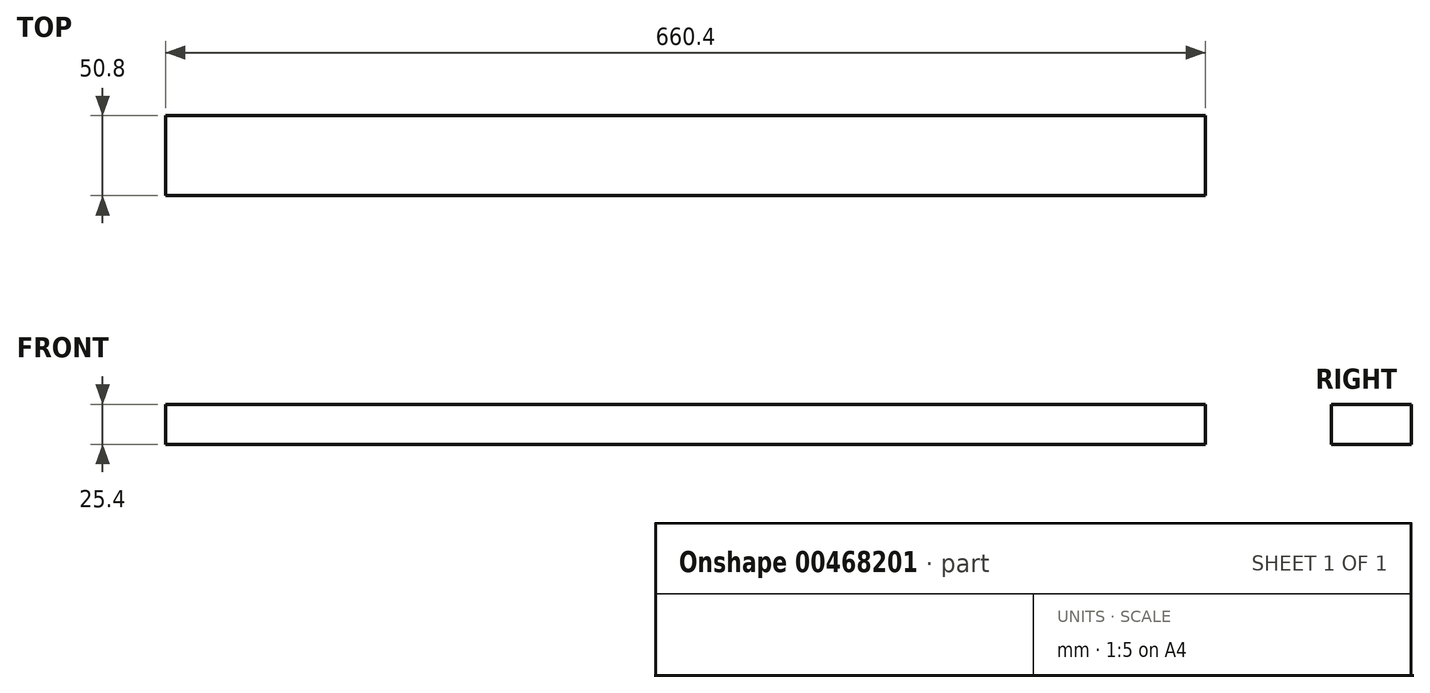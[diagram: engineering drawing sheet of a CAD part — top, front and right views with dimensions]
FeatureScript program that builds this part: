
annotation { "Feature Type Name" : "Feature", "Feature Type Description" : "" }
export const myFeature = defineFeature(function(context is Context, id is Id, definition is map)
    precondition{}
    {
        {
            var Q0;
            Q0=qCreatedBy(makeId("Top.planeOp"),FACE);
            var sketch = newSketch(context, id + "F0", { "sketchPlane" : qUnion([Q0])});
            skLineSegment(sketch, "E0.bottom", {"start": v(0, 0) * mm, "end": v(660.4, 0) * mm});
            skLineSegment(sketch, "E0.top", {"start": v(0, 50.8) * mm, "end": v(660.4, 50.8) * mm});
            skLineSegment(sketch, "E0.left", {"start": v(0, 0) * mm, "end": v(0, 50.8) * mm});
            skLineSegment(sketch, "E0.right", {"start": v(660.4, 0) * mm, "end": v(660.4, 50.8) * mm});
            skSolve(sketch);
        }
        {
            var Q0;
            Q0=makeQuery(id+"F0.imprint","IMPRINT",FACE,{"disambiguationData":[TD([[makeQuery(id+"F0.imprint","IMPRINT",EDGE,{"derivedFrom":sQuery(id+"F0.wireOp",EDGE,"E0.bottom")}),1.0]])]});
            extrude(context, id + "F1", {"entities" : qUnion([Q0]), "depth" : 25.4 * mm});
        }
    });
